# Revit family: QF_ELECTROLUXPROFESSIONAL_1L0A46_TE1120_E
name_source: partatom
category: Attrezzature speciali
units: mm (PartAtom-declared; Revit-internal decimal feet)

## family parameters
Basato su piano di lavoro = No
Condiviso = No
Punto di calcolo locali = No
Quota connettore circolare = Usa diametro
Sempre verticale = Sì
Taglio con vuoti quando caricato = No
Tipo di parte = Normale

## types (7) — shared parameters
Depth = 625 mm
Depth Actual = 625 mm
Height = 850 mm  [stored 2.78871 ft]
Height Actual = 850 mm  [stored 2.78871 ft]
Latent Heat Output = 0.0
Length Actual = 596 mm
Modello = TE1120
Phase = 1
Produttore = Electrolux Professional
Sensible Heat Output = 0.0
URL = www.electroluxprofessional.com
Weight = 44
Width = 597 mm
zero-valued in all types: Gas KW, Prospetto di default, Steam Pounds per Hour

## per-type parameters (varying)
| type | Cycle | Descrizione | Item Number | Volts | Watts |
| 916097781 | 60 Hz | myPRO SMART PROFESSIONAL TUMBLE DRYER TE1120 8KG CONDENSE 200/60/1N 2,8KW JP SST/DARK BLUE | 1L0BJF | 200 V | 2200 W |
| 916097782 | 60 Hz | myPRO SMART PROFESSIONAL TUMBLE DRYER TE1120 8KG CONDENSE 230/60/1N 2,8KW SYMBOLS SCHUKO SST/DARK BLUE | 1L0BJG | 230 V | 2800 W |
| 916097778 | 50 Hz | myPRO SMART PROFESSIONAL TUMBLE DRYER TE1120 8KG CONDENSE 230-240/50/1N 2,8KW EN PLUG-AU SST/DARK BLUE | 1L0BJC | 230 V | 2800 W |
| 916097621 | 50 Hz | myPRO SMART PROFESSIONAL TUMBLE DRYER TE1120 8KG CONDENSE 230/50/1N 2,8KW FR SCHUKO SST/DARK BLUE | 1L0AD7 | 230 V | 2800 W |
| 916097623 | 50 Hz | myPRO SMART PROFESSIONAL TUMBLE DRYER TE1120 8KG CONDENSE 230-240/50/1N 2,8KW EN PLUG-UK SST/DARK BLUE | 1L0AD9 | 230 V | 2800 W |
| 916097622 | 50 Hz | myPRO SMART PROFESSIONAL TUMBLE DRYER TE1120 8KG CONDENSE 230/50/1N 2,8KW DE SCHUKO SST/DARK BLUE | 1L0AD8 | 230 V | 2800 W |
| 916097681 | 50 Hz | myPRO SMART PROFESSIONAL TUMBLE DRYER TE1120 8KG CONDENSE 230/50/1N 2,8KW SYMBOLS SCHUKO SST/DARK BLUE | 1L0AEF | 230 V | 2800 W |

note: [stored X ft] marks values corroborated as IEEE doubles in the binary element streams (Revit-internal decimal feet)

## geometry (parser evidence)
native form markers: Sweep x2
no freeform markers — native parametric forms only
